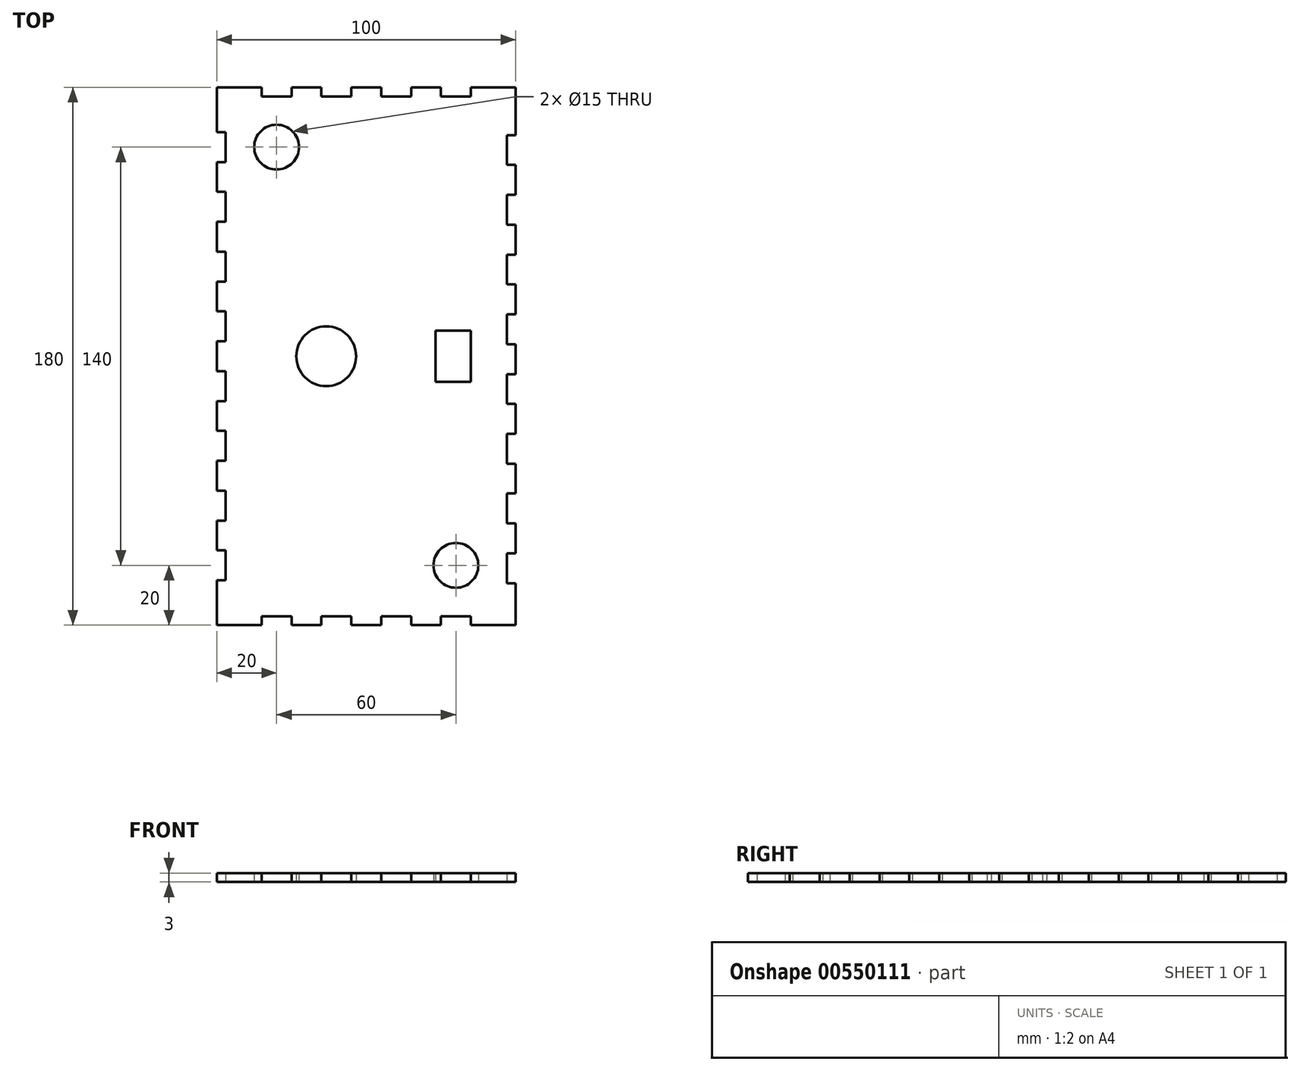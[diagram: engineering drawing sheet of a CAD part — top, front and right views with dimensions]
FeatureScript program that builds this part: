
annotation { "Feature Type Name" : "Feature", "Feature Type Description" : "" }
export const myFeature = defineFeature(function(context is Context, id is Id, definition is map)
    precondition{}
    {
        {
            var Q0;
            Q0=qCreatedBy(makeId("Top.planeOp"),FACE);
            var sketch = newSketch(context, id + "F0", { "sketchPlane" : qUnion([Q0])});
            skPoint(sketch, "E0", {"position": v(0, 0) * mm});
            skLineSegment(sketch, "E1", {"start": v(-47, -5) * mm, "end": v(-44, -5) * mm});
            skLineSegment(sketch, "E2", {"start": v(-44, -5) * mm, "end": v(-44, -15) * mm});
            skLineSegment(sketch, "E3", {"start": v(-44, -15) * mm, "end": v(-47, -15) * mm});
            skLineSegment(sketch, "E4", {"start": v(-47, -15) * mm, "end": v(-47, -25) * mm});
            skLineSegment(sketch, "E5", {"start": v(-47, -25) * mm, "end": v(-44, -25) * mm});
            skLineSegment(sketch, "E6", {"start": v(-44, -25) * mm, "end": v(-44, -35) * mm});
            skLineSegment(sketch, "E7", {"start": v(-44, -35) * mm, "end": v(-47, -35) * mm});
            skLineSegment(sketch, "E8", {"start": v(-47, -35) * mm, "end": v(-47, -45) * mm});
            skLineSegment(sketch, "E9", {"start": v(-47, -45) * mm, "end": v(-44, -45) * mm});
            skLineSegment(sketch, "E10", {"start": v(-44, -45) * mm, "end": v(-44, -55) * mm});
            skLineSegment(sketch, "E11", {"start": v(-44, -55) * mm, "end": v(-47, -55) * mm});
            skLineSegment(sketch, "E12", {"start": v(-47, -55) * mm, "end": v(-47, -65) * mm});
            skLineSegment(sketch, "E13", {"start": v(-47, -65) * mm, "end": v(-44, -65) * mm});
            skLineSegment(sketch, "E14", {"start": v(-44, -65) * mm, "end": v(-44, -75) * mm});
            skLineSegment(sketch, "E15", {"start": v(-44, -75) * mm, "end": v(-47, -75) * mm});
            skLineSegment(sketch, "E16", {"start": v(-47, -75) * mm, "end": v(-47, -90) * mm});
            skLineSegment(sketch, "E17", {"start": v(-47, -5) * mm, "end": v(-47, 0) * mm});
            skLineSegment(sketch, "E18.MirrorCS", {"start": v(-44, 35) * mm, "end": v(-47, 35) * mm});
            skLineSegment(sketch, "E19.MirrorCS", {"start": v(-44, 55) * mm, "end": v(-47, 55) * mm});
            skLineSegment(sketch, "E20.MirrorCS", {"start": v(-44, 15) * mm, "end": v(-47, 15) * mm});
            skLineSegment(sketch, "E21.MirrorCS", {"start": v(-47, 5) * mm, "end": v(-44, 5) * mm});
            skLineSegment(sketch, "E22.MirrorCS", {"start": v(-44, 75) * mm, "end": v(-47, 75) * mm});
            skLineSegment(sketch, "E23.MirrorCS", {"start": v(-47, 45) * mm, "end": v(-44, 45) * mm});
            skLineSegment(sketch, "E24.MirrorCS", {"start": v(-47, 25) * mm, "end": v(-44, 25) * mm});
            skLineSegment(sketch, "E25.MirrorCS", {"start": v(-47, 65) * mm, "end": v(-44, 65) * mm});
            skLineSegment(sketch, "E26.MirrorCS", {"start": v(-44, 25) * mm, "end": v(-44, 35) * mm});
            skLineSegment(sketch, "E27.MirrorCS", {"start": v(-47, 55) * mm, "end": v(-47, 65) * mm});
            skLineSegment(sketch, "E28.MirrorCS", {"start": v(-47, 35) * mm, "end": v(-47, 45) * mm});
            skLineSegment(sketch, "E29.MirrorCS", {"start": v(-47, 15) * mm, "end": v(-47, 25) * mm});
            skLineSegment(sketch, "E30.MirrorCS", {"start": v(-47, 5) * mm, "end": v(-47, 0) * mm});
            skLineSegment(sketch, "E31.MirrorCS", {"start": v(-44, 65) * mm, "end": v(-44, 75) * mm});
            skLineSegment(sketch, "E32.MirrorCS", {"start": v(-47, 75) * mm, "end": v(-47, 90) * mm});
            skLineSegment(sketch, "E33.MirrorCS", {"start": v(-44, 45) * mm, "end": v(-44, 55) * mm});
            skLineSegment(sketch, "E34.MirrorCS", {"start": v(-44, 5) * mm, "end": v(-44, 15) * mm});
            skLineSegment(sketch, "E35", {"start": v(53, 90) * mm, "end": v(38, 90) * mm});
            skLineSegment(sketch, "E36", {"start": v(38, 90) * mm, "end": v(38, 87) * mm});
            skLineSegment(sketch, "E37", {"start": v(38, 87) * mm, "end": v(28, 87) * mm});
            skLineSegment(sketch, "E38", {"start": v(28, 87) * mm, "end": v(28, 90) * mm});
            skLineSegment(sketch, "E39", {"start": v(28, 90) * mm, "end": v(18, 90) * mm});
            skLineSegment(sketch, "E40", {"start": v(18, 90) * mm, "end": v(18, 87) * mm});
            skLineSegment(sketch, "E41", {"start": v(18, 87) * mm, "end": v(8, 87) * mm});
            skLineSegment(sketch, "E42", {"start": v(8, 87) * mm, "end": v(8, 90) * mm});
            skLineSegment(sketch, "E43", {"start": v(8, 90) * mm, "end": v(-2, 90) * mm});
            skLineSegment(sketch, "E44", {"start": v(-2, 90) * mm, "end": v(-2, 87) * mm});
            skLineSegment(sketch, "E45", {"start": v(-2, 87) * mm, "end": v(-12, 87) * mm});
            skLineSegment(sketch, "E46", {"start": v(-12, 87) * mm, "end": v(-12, 90) * mm});
            skLineSegment(sketch, "E47", {"start": v(-12, 90) * mm, "end": v(-22, 90) * mm});
            skLineSegment(sketch, "E48", {"start": v(-22, 90) * mm, "end": v(-22, 87) * mm});
            skLineSegment(sketch, "E49", {"start": v(-22, 87) * mm, "end": v(-32, 87) * mm});
            skLineSegment(sketch, "E50", {"start": v(-32, 87) * mm, "end": v(-32, 90) * mm});
            skLineSegment(sketch, "E51", {"start": v(-32, 90) * mm, "end": v(-47, 90) * mm});
            skLineSegment(sketch, "E52", {"start": v(-47, -90) * mm, "end": v(-32, -90) * mm});
            skLineSegment(sketch, "E53", {"start": v(-32, -90) * mm, "end": v(-32, -87) * mm});
            skLineSegment(sketch, "E54", {"start": v(-32, -87) * mm, "end": v(-22, -87) * mm});
            skLineSegment(sketch, "E55", {"start": v(-22, -87) * mm, "end": v(-22, -90) * mm});
            skLineSegment(sketch, "E56", {"start": v(-22, -90) * mm, "end": v(-12, -90) * mm});
            skLineSegment(sketch, "E57", {"start": v(-12, -90) * mm, "end": v(-12, -87) * mm});
            skLineSegment(sketch, "E58", {"start": v(-12, -87) * mm, "end": v(-2, -87) * mm});
            skLineSegment(sketch, "E59", {"start": v(-2, -87) * mm, "end": v(-2, -90) * mm});
            skLineSegment(sketch, "E60", {"start": v(-2, -90) * mm, "end": v(8, -90) * mm});
            skLineSegment(sketch, "E61", {"start": v(8, -90) * mm, "end": v(8, -87) * mm});
            skLineSegment(sketch, "E62", {"start": v(8, -87) * mm, "end": v(18, -87) * mm});
            skLineSegment(sketch, "E63", {"start": v(18, -87) * mm, "end": v(18, -90) * mm});
            skLineSegment(sketch, "E64", {"start": v(18, -90) * mm, "end": v(28, -90) * mm});
            skLineSegment(sketch, "E65", {"start": v(28, -90) * mm, "end": v(28, -87) * mm});
            skLineSegment(sketch, "E66", {"start": v(28, -87) * mm, "end": v(38, -87) * mm});
            skLineSegment(sketch, "E67", {"start": v(38, -87) * mm, "end": v(38, -90) * mm});
            skLineSegment(sketch, "E68", {"start": v(38, -90) * mm, "end": v(53, -90) * mm});
            skLineSegment(sketch, "E69", {"start": v(53, 4.03) * mm, "end": v(50, 4.03) * mm});
            skLineSegment(sketch, "E70", {"start": v(50, 4.03) * mm, "end": v(50, 14.03) * mm});
            skLineSegment(sketch, "E71", {"start": v(50, 14.03) * mm, "end": v(53, 14.03) * mm});
            skLineSegment(sketch, "E72", {"start": v(53, 14.03) * mm, "end": v(53, 24.03) * mm});
            skLineSegment(sketch, "E73", {"start": v(53, 24.03) * mm, "end": v(50, 24.03) * mm});
            skLineSegment(sketch, "E74", {"start": v(50, 24.03) * mm, "end": v(50, 34.03) * mm});
            skLineSegment(sketch, "E75", {"start": v(50, 34.03) * mm, "end": v(53, 34.03) * mm});
            skLineSegment(sketch, "E76", {"start": v(53, 34.03) * mm, "end": v(53, 44.03) * mm});
            skLineSegment(sketch, "E77", {"start": v(53, 44.03) * mm, "end": v(50, 44.03) * mm});
            skLineSegment(sketch, "E78", {"start": v(50, 44.03) * mm, "end": v(50, 54.03) * mm});
            skLineSegment(sketch, "E79", {"start": v(50, 54.03) * mm, "end": v(53, 54.03) * mm});
            skLineSegment(sketch, "E80", {"start": v(53, 54.03) * mm, "end": v(53, 64.03) * mm});
            skLineSegment(sketch, "E81", {"start": v(53, 64.03) * mm, "end": v(50, 64.03) * mm});
            skLineSegment(sketch, "E82", {"start": v(50, 64.03) * mm, "end": v(50, 74.03) * mm});
            skLineSegment(sketch, "E83", {"start": v(50, 74.03) * mm, "end": v(53, 74.03) * mm});
            skLineSegment(sketch, "E84", {"start": v(53, 74.03) * mm, "end": v(53, 90) * mm});
            skLineSegment(sketch, "E85", {"start": v(53, 4.03) * mm, "end": v(53, 0) * mm});
            skLineSegment(sketch, "E86.MirrorCS", {"start": v(50, -35.97) * mm, "end": v(53, -35.97) * mm});
            skLineSegment(sketch, "E87.MirrorCS", {"start": v(50, -55.97) * mm, "end": v(53, -55.97) * mm});
            skLineSegment(sketch, "E88.MirrorCS", {"start": v(50, -15.97) * mm, "end": v(53, -15.97) * mm});
            skLineSegment(sketch, "E89.MirrorCS", {"start": v(53, -5.97) * mm, "end": v(50, -5.97) * mm});
            skLineSegment(sketch, "E90.MirrorCS", {"start": v(50, -75.97) * mm, "end": v(53, -75.97) * mm});
            skLineSegment(sketch, "E91.MirrorCS", {"start": v(53, -45.97) * mm, "end": v(50, -45.97) * mm});
            skLineSegment(sketch, "E92.MirrorCS", {"start": v(53, -25.97) * mm, "end": v(50, -25.97) * mm});
            skLineSegment(sketch, "E93.MirrorCS", {"start": v(53, -65.97) * mm, "end": v(50, -65.97) * mm});
            skLineSegment(sketch, "E94.MirrorCS", {"start": v(50, -25.97) * mm, "end": v(50, -35.97) * mm});
            skLineSegment(sketch, "E95.MirrorCS", {"start": v(53, -55.97) * mm, "end": v(53, -65.97) * mm});
            skLineSegment(sketch, "E96.MirrorCS", {"start": v(53, -35.97) * mm, "end": v(53, -45.97) * mm});
            skLineSegment(sketch, "E97.MirrorCS", {"start": v(53, -15.97) * mm, "end": v(53, -25.97) * mm});
            skLineSegment(sketch, "E98.MirrorCS", {"start": v(53, -5.97) * mm, "end": v(53, 0) * mm});
            skLineSegment(sketch, "E99.MirrorCS", {"start": v(50, -65.97) * mm, "end": v(50, -75.97) * mm});
            skLineSegment(sketch, "E100.MirrorCS", {"start": v(53, -75.97) * mm, "end": v(53, -90) * mm});
            skLineSegment(sketch, "E101.MirrorCS", {"start": v(50, -45.97) * mm, "end": v(50, -55.97) * mm});
            skLineSegment(sketch, "E102.MirrorCS", {"start": v(50, -5.97) * mm, "end": v(50, -15.97) * mm});
            skLineSegment(sketch, "E103.bottom", {"start": v(26.2, 8.55) * mm, "end": v(38, 8.55) * mm});
            skLineSegment(sketch, "E103.top", {"start": v(26.2, -8.55) * mm, "end": v(38, -8.55) * mm});
            skLineSegment(sketch, "E103.left", {"start": v(26.2, 8.55) * mm, "end": v(26.2, -8.55) * mm});
            skLineSegment(sketch, "E103.right", {"start": v(38, 8.55) * mm, "end": v(38, -8.55) * mm});
            skCircle(sketch, "E104", {"center": v(-27, 70) * mm, "radius": 7.5 * mm});
            skCircle(sketch, "E105", {"center": v(33, -70) * mm, "radius": 7.5 * mm});
            skCircle(sketch, "E106", {"center": v(-10.4, 0) * mm, "radius": 10 * mm});
            skSolve(sketch);
        }
        {
            var Q0;
            Q0=qSketchRegion(id+"F0",true);
            extrude(context, id + "F1", {"entities" : qUnion([Q0]), "depth" : 3 * mm, "offsetDistance" : 25 * mm, "symmetric" : true});
        }
    });
